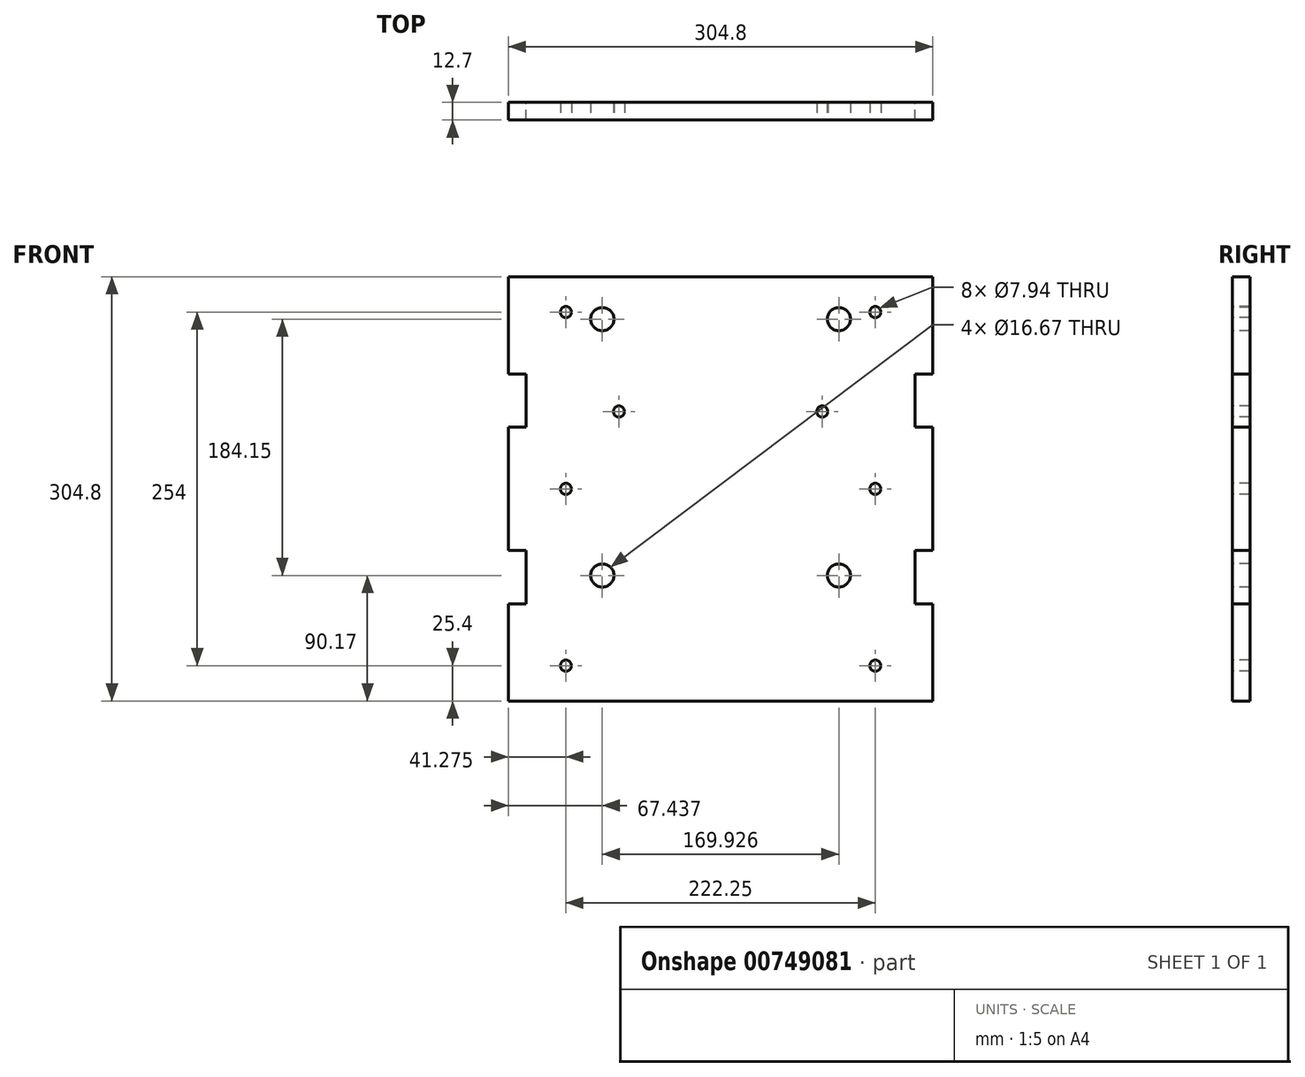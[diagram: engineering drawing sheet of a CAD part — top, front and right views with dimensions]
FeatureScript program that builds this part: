
annotation { "Feature Type Name" : "Feature", "Feature Type Description" : "" }
export const myFeature = defineFeature(function(context is Context, id is Id, definition is map)
    precondition{}
    {
        {
            var Q0;
            Q0=qCreatedBy(makeId("Front.planeOp"),FACE);
            var sketch = newSketch(context, id + "F0", { "sketchPlane" : qUnion([Q0])});
            skLineSegment(sketch, "E0.bottom", {"start": v(482.6, 0) * mm, "end": v(177.8, 0) * mm});
            skLineSegment(sketch, "E0.top", {"start": v(482.6, 304.8) * mm, "end": v(177.8, 304.8) * mm});
            skLineSegment(sketch, "E0.left", {"start": v(482.6, 0) * mm, "end": v(482.6, 69.85) * mm});
            skLineSegment(sketch, "E0.right", {"start": v(177.8, 0) * mm, "end": v(177.8, 69.85) * mm});
            skLineSegment(sketch, "E1", {"start": v(330.2, 304.8) * mm, "end": v(330.2, 0) * mm, "construction": true});
            skLineSegment(sketch, "E2", {"start": v(441.33, 304.8) * mm, "end": v(441.33, 0) * mm, "construction": true});
            skPoint(sketch, "E3", {"position": v(441.32, 279.4) * mm});
            skLineSegment(sketch, "E4", {"start": v(482.6, 152.4) * mm, "end": v(177.8, 152.4) * mm, "construction": true});
            skPoint(sketch, "E5", {"position": v(441.33, 152.4) * mm});
            skPoint(sketch, "E6.MirrorP", {"position": v(441.33, 25.4) * mm});
            skLineSegment(sketch, "E7", {"start": v(415.16, 152.4) * mm, "end": v(415.16, 304.8) * mm, "construction": true});
            skPoint(sketch, "E8", {"position": v(415.16, 274.32) * mm});
            skLineSegment(sketch, "E9", {"start": v(415.16, 228.6) * mm, "end": v(415.16, 9.47) * mm, "construction": true});
            skPoint(sketch, "E10", {"position": v(415.16, 90.17) * mm});
            skPoint(sketch, "E11.MirrorP", {"position": v(245.24, 274.32) * mm});
            skPoint(sketch, "E12.MirrorP", {"position": v(245.24, 90.17) * mm});
            skPoint(sketch, "E13.MirrorP", {"position": v(219.07, 279.4) * mm});
            skPoint(sketch, "E14.MirrorP", {"position": v(219.07, 152.4) * mm});
            skPoint(sketch, "E15.MirrorP", {"position": v(219.07, 25.4) * mm});
            skLineSegment(sketch, "E16.bottom", {"start": v(177.8, 234.95) * mm, "end": v(190.55, 234.95) * mm});
            skLineSegment(sketch, "E16.top", {"start": v(177.8, 196.75) * mm, "end": v(190.55, 196.75) * mm});
            skLineSegment(sketch, "E16.right", {"start": v(190.55, 234.95) * mm, "end": v(190.55, 196.75) * mm});
            skLineSegment(sketch, "E17.MirrorCS", {"start": v(469.85, 234.95) * mm, "end": v(469.85, 196.75) * mm});
            skLineSegment(sketch, "E18.MirrorCS", {"start": v(482.6, 234.95) * mm, "end": v(469.85, 234.95) * mm});
            skLineSegment(sketch, "E19.MirrorCS", {"start": v(482.6, 196.75) * mm, "end": v(469.85, 196.75) * mm});
            skLineSegment(sketch, "E20.MirrorCS", {"start": v(190.55, 69.85) * mm, "end": v(190.55, 108.05) * mm});
            skLineSegment(sketch, "E21.MirrorCS", {"start": v(177.8, 69.85) * mm, "end": v(190.55, 69.85) * mm});
            skLineSegment(sketch, "E22.MirrorCS", {"start": v(177.8, 108.05) * mm, "end": v(190.55, 108.05) * mm});
            skLineSegment(sketch, "E23.MirrorCS", {"start": v(469.85, 69.85) * mm, "end": v(469.85, 108.05) * mm});
            skLineSegment(sketch, "E24.MirrorCS", {"start": v(482.6, 69.85) * mm, "end": v(469.85, 69.85) * mm});
            skLineSegment(sketch, "E25.MirrorCS", {"start": v(482.6, 108.05) * mm, "end": v(469.85, 108.05) * mm});
            skLineSegment(sketch, "E26.trimOffspring", {"start": v(177.8, 234.95) * mm, "end": v(177.8, 304.8) * mm});
            skLineSegment(sketch, "E27.trimOffspring", {"start": v(482.6, 234.95) * mm, "end": v(482.6, 304.8) * mm});
            skLineSegment(sketch, "E28.trimOffspring", {"start": v(482.6, 108.05) * mm, "end": v(482.6, 196.75) * mm});
            skLineSegment(sketch, "E29.trimOffspring", {"start": v(177.8, 108.05) * mm, "end": v(177.8, 196.75) * mm});
            skLineSegment(sketch, "E30", {"start": v(177.8, 207.96) * mm, "end": v(330.2, 207.96) * mm, "construction": true});
            skPoint(sketch, "E31", {"position": v(257.18, 207.96) * mm});
            skPoint(sketch, "E32.MirrorP", {"position": v(403.23, 207.96) * mm});
            skSolve(sketch);
        }
        {
            var Q0;
            Q0 = qSketchRegion(id + "F0", true);
            extrude(context, id + "F1", {"entities" : qUnion([Q0]), "depth" : 12.7 * mm, "offsetDistance" : 25.4 * mm});
        }
        {
            var Q0;
            Q0=sQuery(id+"F0.wireOp",VERTEX,"E11.MirrorP");
            var Q1;
            Q1=sQuery(id+"F0.wireOp",VERTEX,"E8");
            var Q2;
            Q2=sQuery(id+"F0.wireOp",VERTEX,"E10");
            var Q3;
            Q3=sQuery(id+"F0.wireOp",VERTEX,"E12.MirrorP");
            var Q4;
            Q4=makeQuery(id+"F1.opExtrude","SWEPT_BODY",BODY,{"disambiguationData":[OSD([sQuery(id+"F0.wireOp",EDGE,"E0.bottom"),sQuery(id+"F0.wireOp",EDGE,"E0.top"),sQuery(id+"F0.wireOp",EDGE,"E0.left"),sQuery(id+"F0.wireOp",EDGE,"E0.right"),sQuery(id+"F0.wireOp",EDGE,"E16.bottom"),sQuery(id+"F0.wireOp",EDGE,"E16.top"),sQuery(id+"F0.wireOp",EDGE,"E16.right"),sQuery(id+"F0.wireOp",EDGE,"E17.MirrorCS"),sQuery(id+"F0.wireOp",EDGE,"E18.MirrorCS"),sQuery(id+"F0.wireOp",EDGE,"E19.MirrorCS"),sQuery(id+"F0.wireOp",EDGE,"E20.MirrorCS"),sQuery(id+"F0.wireOp",EDGE,"E21.MirrorCS"),sQuery(id+"F0.wireOp",EDGE,"E22.MirrorCS"),sQuery(id+"F0.wireOp",EDGE,"E23.MirrorCS"),sQuery(id+"F0.wireOp",EDGE,"E24.MirrorCS"),sQuery(id+"F0.wireOp",EDGE,"E25.MirrorCS"),sQuery(id+"F0.wireOp",EDGE,"E26.trimOffspring"),sQuery(id+"F0.wireOp",EDGE,"E27.trimOffspring"),sQuery(id+"F0.wireOp",EDGE,"E28.trimOffspring"),sQuery(id+"F0.wireOp",EDGE,"E29.trimOffspring")])]});
            hole(context, id + "F2", {"style" : HoleStyle.SIMPLE, "endStyle" : HoleEndStyle.BLIND, "oppositeDirection" : true, "standardTappedOrClearance" : lookupTablePath({ "fit" : "Normal (ASME)", "standard" : "ANSI", "size" : "5/8", "type" : "Clearance" }), "standardBlindInLast" : lookupTablePath({ "fit" : "Free", "standard" : "ANSI", "size" : "5/8", "type" : "Clearance" }), "holeDiameter" : 16.67 * mm, "majorDiameter" : 15.88 * mm, "holeDepth" : 12.7 * mm, "isTappedThrough" : true, "tappedDepth" : 15.9 * mm, "tapClearance" : 3, "locations" : qUnion([Q0, Q1, Q2, Q3]), "scope" : qUnion([Q4])});
        }
        {
            var Q0;
            Q0=sQuery(id+"F0.wireOp",VERTEX,"E13.MirrorP");
            var Q1;
            Q1=sQuery(id+"F0.wireOp",VERTEX,"E31");
            var Q2;
            Q2=sQuery(id+"F0.wireOp",VERTEX,"E14.MirrorP");
            var Q3;
            Q3=sQuery(id+"F0.wireOp",VERTEX,"E32.MirrorP");
            var Q4;
            Q4=sQuery(id+"F0.wireOp",VERTEX,"E3");
            var Q5;
            Q5=sQuery(id+"F0.wireOp",VERTEX,"E5");
            var Q6;
            Q6=sQuery(id+"F0.wireOp",VERTEX,"E6.MirrorP");
            var Q7;
            Q7=sQuery(id+"F0.wireOp",VERTEX,"E15.MirrorP");
            var Q8;
            Q8=makeQuery(id+"F1.opExtrude","SWEPT_BODY",BODY,{"disambiguationData":[OSD([sQuery(id+"F0.wireOp",EDGE,"E0.bottom"),sQuery(id+"F0.wireOp",EDGE,"E0.top"),sQuery(id+"F0.wireOp",EDGE,"E0.left"),sQuery(id+"F0.wireOp",EDGE,"E0.right"),sQuery(id+"F0.wireOp",EDGE,"E16.bottom"),sQuery(id+"F0.wireOp",EDGE,"E16.top"),sQuery(id+"F0.wireOp",EDGE,"E16.right"),sQuery(id+"F0.wireOp",EDGE,"E17.MirrorCS"),sQuery(id+"F0.wireOp",EDGE,"E18.MirrorCS"),sQuery(id+"F0.wireOp",EDGE,"E19.MirrorCS"),sQuery(id+"F0.wireOp",EDGE,"E20.MirrorCS"),sQuery(id+"F0.wireOp",EDGE,"E21.MirrorCS"),sQuery(id+"F0.wireOp",EDGE,"E22.MirrorCS"),sQuery(id+"F0.wireOp",EDGE,"E23.MirrorCS"),sQuery(id+"F0.wireOp",EDGE,"E24.MirrorCS"),sQuery(id+"F0.wireOp",EDGE,"E25.MirrorCS"),sQuery(id+"F0.wireOp",EDGE,"E26.trimOffspring"),sQuery(id+"F0.wireOp",EDGE,"E27.trimOffspring"),sQuery(id+"F0.wireOp",EDGE,"E28.trimOffspring"),sQuery(id+"F0.wireOp",EDGE,"E29.trimOffspring")])]});
            hole(context, id + "F3", {"style" : HoleStyle.SIMPLE, "endStyle" : HoleEndStyle.BLIND, "oppositeDirection" : true, "standardTappedOrClearance" : lookupTablePath({ "standard" : "ANSI", "engagement" : "75%", "pitch" : "16 tpi", "size" : "3/8", "type" : "Tapped" }), "standardBlindInLast" : lookupTablePath({ "standard" : "ANSI", "engagement" : "75%", "pitch" : "16 tpi", "size" : "3/8", "type" : "Tapped" }), "holeDiameter" : 7.94 * mm, "majorDiameter" : 9.52 * mm, "showTappedDepth" : true, "holeDepth" : 17.46 * mm, "isTappedThrough" : true, "tappedDepth" : 12.7 * mm, "tapClearance" : 3, "locations" : qUnion([Q0, Q1, Q2, Q3, Q4, Q5, Q6, Q7]), "scope" : qUnion([Q8])});
        }
    });
